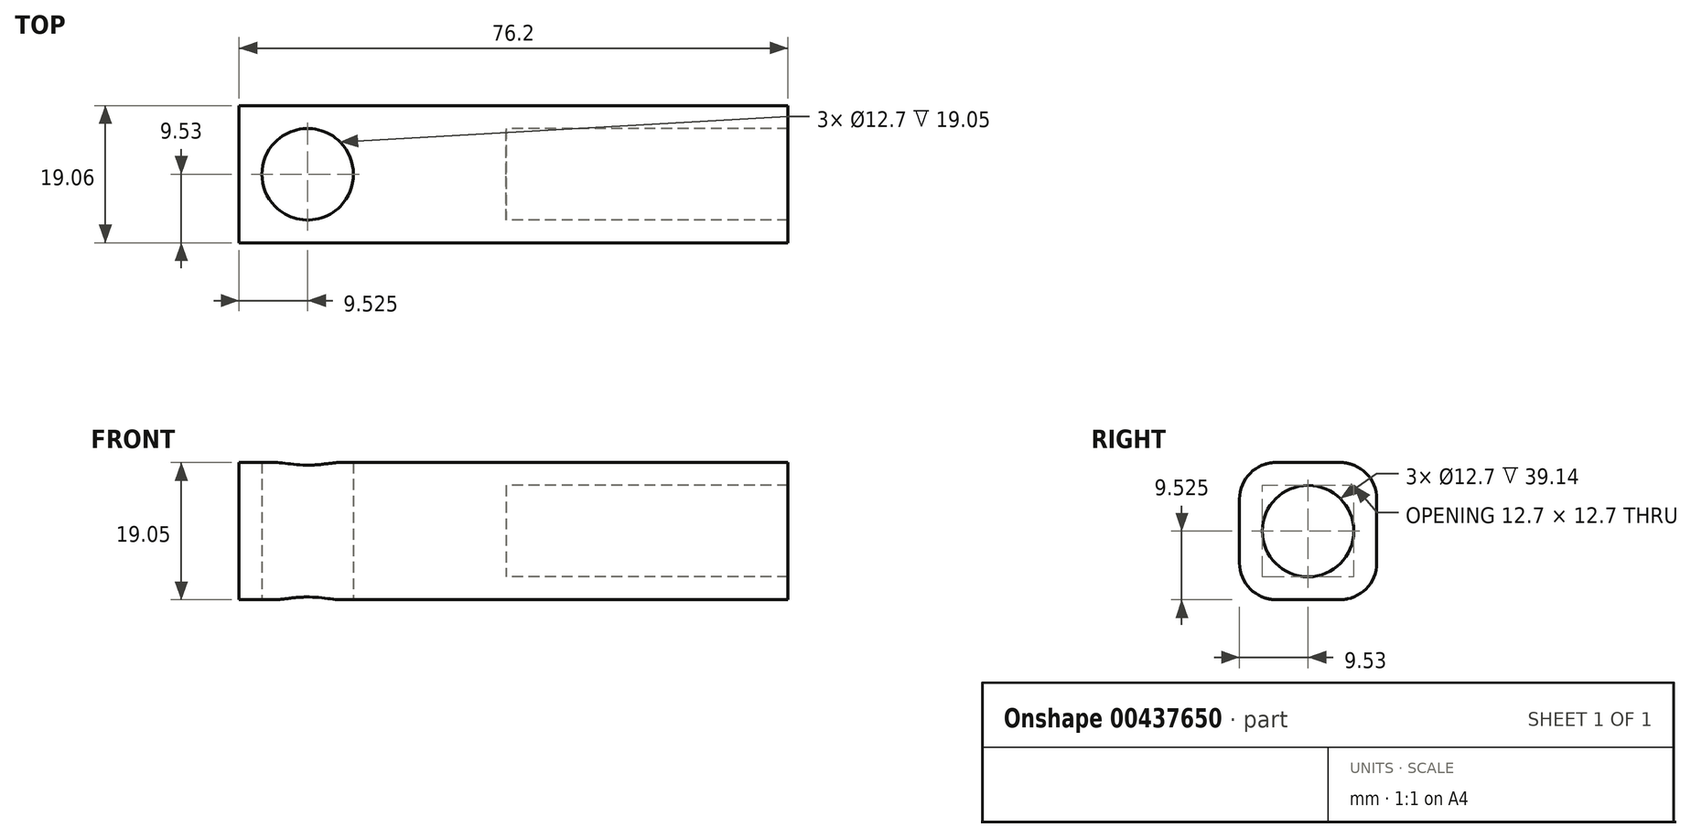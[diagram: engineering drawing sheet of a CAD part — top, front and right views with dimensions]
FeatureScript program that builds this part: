
annotation { "Feature Type Name" : "Feature", "Feature Type Description" : "" }
export const myFeature = defineFeature(function(context is Context, id is Id, definition is map)
    precondition{}
    {
        {
            var Q0;
            Q0=qCreatedBy(makeId("Top.planeOp"),FACE);
            var sketch = newSketch(context, id + "F0", { "sketchPlane" : qUnion([Q0])});
            skLineSegment(sketch, "E0.bottom", {"start": v(39.14, 9.53) * mm, "end": v(-37.06, 9.53) * mm});
            skLineSegment(sketch, "E0.top", {"start": v(39.14, -9.53) * mm, "end": v(-37.06, -9.53) * mm});
            skLineSegment(sketch, "E0.left", {"start": v(39.14, 9.53) * mm, "end": v(39.14, -9.53) * mm});
            skLineSegment(sketch, "E0.right", {"start": v(-37.06, 9.53) * mm, "end": v(-37.06, -9.53) * mm});
            skPoint(sketch, "E0.middle", {"position": v(1.04, 0) * mm});
            skSolve(sketch);
        }
        {
            var Q0;
            Q0 = qSketchRegion(id + "F0", true);
            extrude(context, id + "F1", {"entities" : qUnion([Q0]), "depth" : 19.05 * mm});
        }
        {
            var Q0;
            Q0=qCreatedBy(makeId("Right.planeOp"),FACE);
            var sketch = newSketch(context, id + "F2", { "sketchPlane" : qUnion([Q0])});
            skPoint(sketch, "E1", {"position": v(0, 9.53) * mm});
            skSolve(sketch);
        }
        {
            var Q0;
            Q0=sQuery(id+"F2.wireOp",VERTEX,"E1");
            var Q1;
            Q1=makeQuery(id+"F1.opExtrude","SWEPT_BODY",BODY,{"disambiguationData":[OSD([sQuery(id+"F0.wireOp",EDGE,"E0.bottom"),sQuery(id+"F0.wireOp",EDGE,"E0.top"),sQuery(id+"F0.wireOp",EDGE,"E0.left"),sQuery(id+"F0.wireOp",EDGE,"E0.right")])]});
            hole(context, id + "F3", {"style" : HoleStyle.SIMPLE, "endStyle" : HoleEndStyle.THROUGH, "oppositeDirection" : true, "holeDiameter" : 12.7 * mm, "isTappedThrough" : true, "tappedDepth" : 12.7 * mm, "tapClearance" : 3, "locations" : qUnion([Q0]), "scope" : qUnion([Q1])});
        }
        {
            var Q0;
            Q0=qCreatedBy(makeId("Top.planeOp"),FACE);
            var sketch = newSketch(context, id + "F4", { "sketchPlane" : qUnion([Q0])});
            skPoint(sketch, "E2", {"position": v(-27.53, 0) * mm});
            skSolve(sketch);
        }
        {
            var Q0;
            Q0=sQuery(id+"F4.wireOp",VERTEX,"E2");
            var Q1;
            Q1=makeQuery(id+"F1.opExtrude","SWEPT_BODY",BODY,{"disambiguationData":[OSD([sQuery(id+"F0.wireOp",EDGE,"E0.bottom"),sQuery(id+"F0.wireOp",EDGE,"E0.top"),sQuery(id+"F0.wireOp",EDGE,"E0.left"),sQuery(id+"F0.wireOp",EDGE,"E0.right")])]});
            hole(context, id + "F5", {"style" : HoleStyle.SIMPLE, "endStyle" : HoleEndStyle.THROUGH, "oppositeDirection" : true, "holeDiameter" : 12.7 * mm, "isTappedThrough" : true, "tappedDepth" : 12.7 * mm, "tapClearance" : 3, "locations" : qUnion([Q0]), "scope" : qUnion([Q1])});
        }
        {
            var Q0;
            Q0=makeQuery(id+"F1.opExtrude","CAP_EDGE",EDGE,{"disambiguationData":[OSD([sQuery(id+"F0.wireOp",EDGE,"E0.bottom")])],"isStart":false});
            var Q1;
            Q1=makeQuery(id+"F1.opExtrude","CAP_EDGE",EDGE,{"disambiguationData":[OSD([sQuery(id+"F0.wireOp",EDGE,"E0.top")])],"isStart":false});
            var Q2;
            Q2=makeQuery(id+"F1.opExtrude","CAP_EDGE",EDGE,{"disambiguationData":[OSD([sQuery(id+"F0.wireOp",EDGE,"E0.top")])],"isStart":true});
            var Q3;
            Q3=makeQuery(id+"F1.opExtrude","CAP_EDGE",EDGE,{"disambiguationData":[OSD([sQuery(id+"F0.wireOp",EDGE,"E0.bottom")])],"isStart":true});
            fillet(context, id + "F6", {"entities" : qUnion([Q0, Q1, Q2, Q3]), "radius" : 5.08 * mm, "tangentPropagation" : true, "allowEdgeOverflow" : false});
        }
    });
